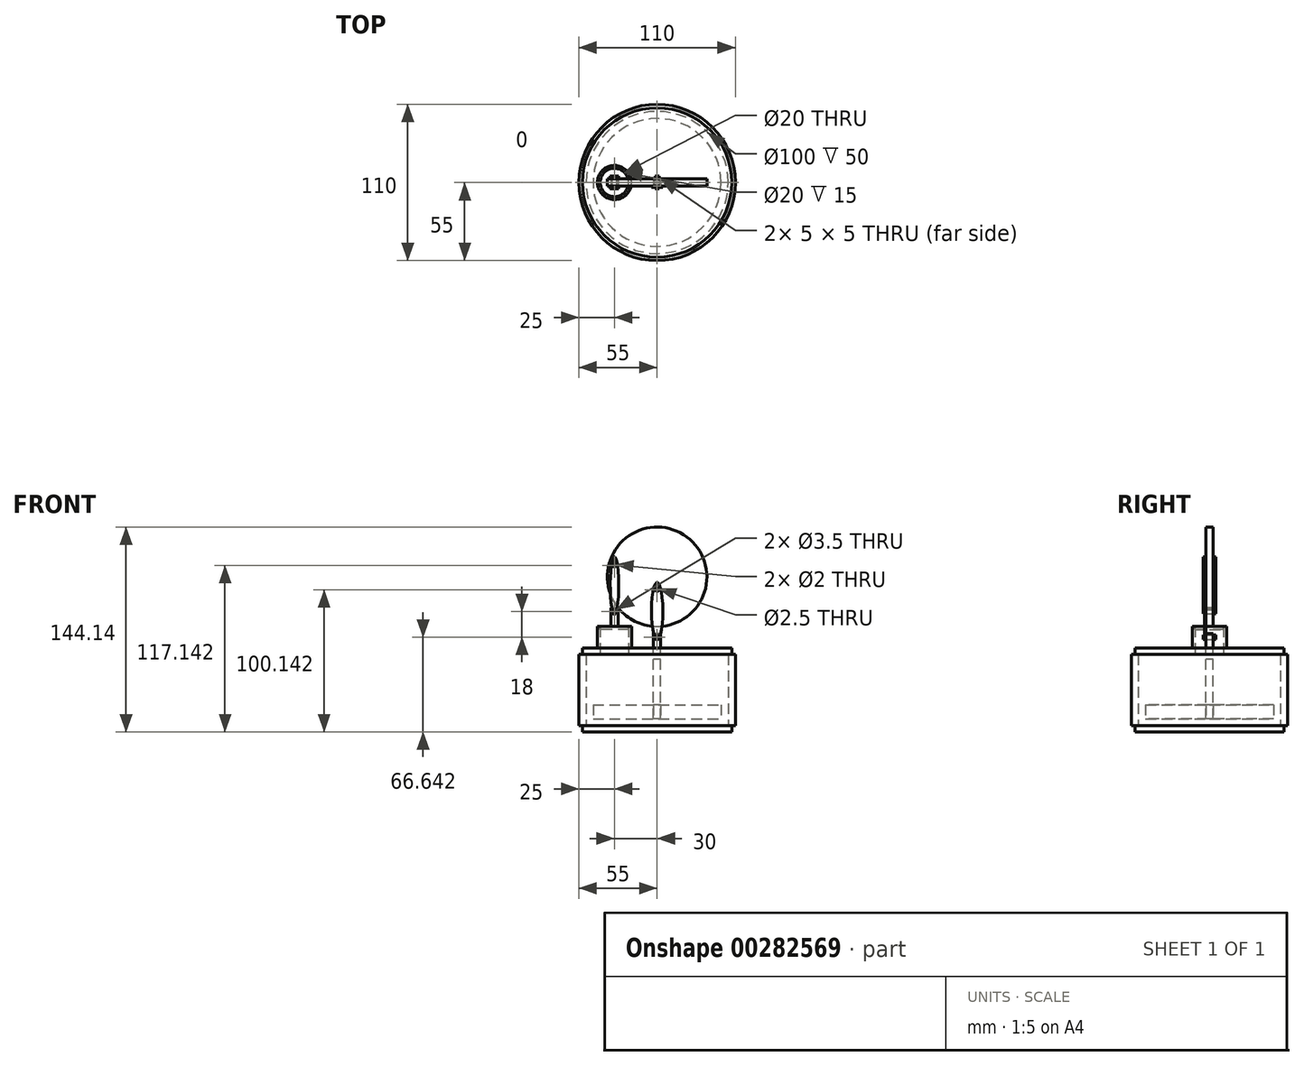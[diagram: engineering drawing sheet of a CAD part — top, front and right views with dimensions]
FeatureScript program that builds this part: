
annotation { "Feature Type Name" : "Feature", "Feature Type Description" : "" }
export const myFeature = defineFeature(function(context is Context, id is Id, definition is map)
    precondition{}
    {
        {
            var Q0;
            Q0=qCreatedBy(makeId("Top.planeOp"),FACE);
            var sketch = newSketch(context, id + "F0", { "sketchPlane" : qUnion([Q0])});
            skCircle(sketch, "E0", {"center": v(0, 0) * mm, "radius": 50 * mm});
            skCircle(sketch, "E1", {"center": v(0, 0) * mm, "radius": 55 * mm});
            skSolve(sketch);
        }
        {
            var Q0;
            Q0=makeQuery(id+"F0.imprint","IMPRINT",FACE,{"disambiguationData":[TD([[makeQuery(id+"F0.imprint","IMPRINT",EDGE,{"derivedFrom":sQuery(id+"F0.wireOp",EDGE,"E0")}),-1.0]])]});
            extrude(context, id + "F1", {"entities" : qUnion([Q0]), "endBound" : BoundingType.SYMMETRIC, "depth" : 50 * mm});
        }
        {
            var Q0;
            Q0=makeQuery(id+"F1.opExtrude","CAP_FACE",FACE,{"disambiguationData":[OSD([sQuery(id+"F0.wireOp",EDGE,"E0"),sQuery(id+"F0.wireOp",EDGE,"E1")])],"isStart":true});
            var sketch = newSketch(context, id + "F2", { "sketchPlane" : qUnion([Q0])});
            skCircle(sketch, "E2", {"center": v(0, 0) * mm, "radius": 52.5 * mm});
            skSolve(sketch);
        }
        {
            var Q0;
            Q0 = qSketchRegion(id + "F2", true);
            extrude(context, id + "F3", {"entities" : qUnion([Q0]), "depth" : 4.57 * mm});
        }
        {
            var Q0;
            Q0=makeQuery(id+"F3.opExtrude","SWEPT_BODY",BODY,{"disambiguationData":[OSD([sQuery(id+"F2.wireOp",EDGE,"E2")])]});
            var Q1;
            Q1=qCreatedBy(makeId("Top.planeOp"),FACE);
            mirror(context, id + "F4", {"entities" : qUnion([Q0]), "mirrorPlane" : qUnion([Q1])});
        }
        {
            var Q0;
            Q0=qCreatedBy(makeId("Front.planeOp"),FACE);
            var sketch = newSketch(context, id + "F5", { "sketchPlane" : qUnion([Q0])});
            skLineSegment(sketch, "E3.bottom", {"start": v(-20, 0) * mm, "end": v(-40, 0) * mm});
            skLineSegment(sketch, "E3.top", {"start": v(-20, 55) * mm, "end": v(-40, 55) * mm});
            skLineSegment(sketch, "E3.left", {"start": v(-20, 0) * mm, "end": v(-20, 55) * mm});
            skLineSegment(sketch, "E3.right", {"start": v(-40, 0) * mm, "end": v(-40, 55) * mm});
            skLineSegment(sketch, "E4", {"start": v(-30, 55) * mm, "end": v(-30, 0) * mm});
            skSolve(sketch);
        }
        {
            var Q0;
            {var subQ0=sQuery(id+"F5.wireOp",EDGE,"E3.right");Q0=makeQuery(id+"F5.imprint","IMPRINT",FACE,{"disambiguationData":[TD([[makeQuery(id+"F5.imprint","IMPRINT",EDGE,{"derivedFrom":subQ0}),-1.0]])]});}
            var Q1;
            Q1=sQuery(id+"F5.wireOp",EDGE,"E4");
            revolve(context, id + "F6", {"operationType" : NewBodyOperationType.REMOVE, "entities" : qUnion([Q0]), "axis" : qUnion([Q1]), "revolveType" : RevolveType.FULL, "oppositeDirection" : true});
        }
        {
            var Q0;
            Q0=makeQuery(id+"F4.opPattern","COPY",FACE,{"derivedFrom":makeQuery(id+"F3.opExtrude","CAP_FACE",FACE,{"disambiguationData":[OSD([sQuery(id+"F2.wireOp",EDGE,"E2")])],"isStart":false}),"instanceName":"1"});
            var sketch = newSketch(context, id + "F7", { "sketchPlane" : qUnion([Q0])});
            skCircle(sketch, "E5", {"center": v(-30, 0) * mm, "radius": 10 * mm});
            skCircle(sketch, "E6", {"center": v(-30, 0) * mm, "radius": 12 * mm});
            skSolve(sketch);
        }
        {
            var Q0;
            Q0=makeQuery(id+"F7.imprint","IMPRINT",FACE,{"disambiguationData":[TD([[makeQuery(id+"F7.imprint","IMPRINT",EDGE,{"derivedFrom":sQuery(id+"F7.wireOp",EDGE,"E5")}),-1.0]])]});
            extrude(context, id + "F8", {"entities" : qUnion([Q0]), "depth" : 15 * mm});
        }
        {
            var Q0;
            Q0=makeQuery(id+"F8.opExtrude","CAP_FACE",FACE,{"disambiguationData":[OSD([sQuery(id+"F7.wireOp",EDGE,"E5"),sQuery(id+"F7.wireOp",EDGE,"E6")])],"isStart":false});
            var sketch = newSketch(context, id + "F9", { "sketchPlane" : qUnion([Q0])});
            skCircle(sketch, "E7", {"center": v(-30, 0) * mm, "radius": 10 * mm});
            skSolve(sketch);
        }
        {
            var Q0;
            Q0 = qSketchRegion(id + "F9", true);
            extrude(context, id + "F10", {"entities" : qUnion([Q0]), "oppositeDirection" : true, "depth" : 2 * mm});
        }
        {
            var Q0;
            Q0=makeQuery(id+"F4.opPattern","COPY",FACE,{"derivedFrom":makeQuery(id+"F3.opExtrude","CAP_FACE",FACE,{"disambiguationData":[OSD([sQuery(id+"F2.wireOp",EDGE,"E2")])],"isStart":false}),"instanceName":"1"});
            var sketch = newSketch(context, id + "F11", { "sketchPlane" : qUnion([Q0])});
            skLineSegment(sketch, "E8.bottom", {"start": v(2.5, 2.5) * mm, "end": v(-2.5, 2.5) * mm});
            skLineSegment(sketch, "E8.top", {"start": v(2.5, -2.5) * mm, "end": v(-2.5, -2.5) * mm});
            skLineSegment(sketch, "E8.left", {"start": v(2.5, 2.5) * mm, "end": v(2.5, -2.5) * mm});
            skLineSegment(sketch, "E8.right", {"start": v(-2.5, 2.5) * mm, "end": v(-2.5, -2.5) * mm});
            skPoint(sketch, "E8.middle", {"position": v(0, 0) * mm});
            skSolve(sketch);
        }
        {
            var Q0;
            Q0=makeQuery(id+"F11.imprint","IMPRINT",FACE,{"disambiguationData":[TD([[makeQuery(id+"F11.imprint","IMPRINT",EDGE,{"derivedFrom":sQuery(id+"F11.wireOp",EDGE,"E8.bottom")}),1.0]])]});
            extrude(context, id + "F12", {"entities" : qUnion([Q0]), "operationType" : NewBodyOperationType.REMOVE, "oppositeDirection" : true, "depth" : 25 * mm});
        }
        {
            var Q0;
            Q0 = qSketchRegion(id + "F11", true);
            extrude(context, id + "F13", {"entities" : qUnion([Q0]), "oppositeDirection" : true, "depth" : 50 * mm, "hasSecondDirection" : true, "secondDirectionOppositeDirection" : false, "secondDirectionDepth" : 10 * mm});
        }
        {
            var Q0;
            Q0=makeQuery(id+"F13.opExtrude","CAP_FACE",FACE,{"disambiguationData":[OSD([sQuery(id+"F11.wireOp",EDGE,"E8.bottom"),sQuery(id+"F11.wireOp",EDGE,"E8.top"),sQuery(id+"F11.wireOp",EDGE,"E8.left"),sQuery(id+"F11.wireOp",EDGE,"E8.right")])],"isStart":false});
            var sketch = newSketch(context, id + "F14", { "sketchPlane" : qUnion([Q0])});
            skCircle(sketch, "E9", {"center": v(0, 0) * mm, "radius": 45 * mm});
            skSolve(sketch);
        }
        {
            var Q0;
            Q0=makeQuery(id+"F14.imprint","IMPRINT",FACE,{"disambiguationData":[TD([[makeQuery(id+"F14.imprint","IMPRINT",EDGE,{"derivedFrom":sQuery(id+"F14.wireOp",EDGE,"E9")}),1.0]])]});
            extrude(context, id + "F15", {"entities" : qUnion([Q0]), "oppositeDirection" : true, "depth" : 10 * mm});
        }
        {
            var Q0;
            Q0=makeQuery(id+"F13.opExtrude","SWEPT_FACE",FACE,{"disambiguationData":[OSD([sQuery(id+"F11.wireOp",EDGE,"E8.top")])]});
            var sketch = newSketch(context, id + "F16", { "sketchPlane" : qUnion([Q0])});
            skLineSegment(sketch, "E10.bottom", {"start": v(-2.5, 39.57) * mm, "end": v(2.5, 39.57) * mm});
            skLineSegment(sketch, "E10.top", {"start": v(-2.5, 34.57) * mm, "end": v(2.5, 34.57) * mm});
            skLineSegment(sketch, "E10.left", {"start": v(-2.5, 39.57) * mm, "end": v(-2.5, 34.57) * mm});
            skLineSegment(sketch, "E10.right", {"start": v(2.5, 39.57) * mm, "end": v(2.5, 34.57) * mm});
            skCircle(sketch, "E11", {"center": v(0, 37.07) * mm, "radius": 1.75 * mm});
            skCircle(sketch, "E12", {"center": v(0, 37.07) * mm, "radius": 1.5 * mm});
            skSolve(sketch);
        }
        {
            var Q0;
            Q0=makeQuery(id+"F16.imprint","IMPRINT",FACE,{"disambiguationData":[TD([[makeQuery(id+"F16.imprint","IMPRINT",EDGE,{"derivedFrom":sQuery(id+"F16.wireOp",EDGE,"E11")}),1.0]])]});
            var Q1;
            Q1=makeQuery(id+"F16.imprint","IMPRINT",FACE,{"disambiguationData":[TD([[makeQuery(id+"F16.imprint","IMPRINT",EDGE,{"derivedFrom":sQuery(id+"F16.wireOp",EDGE,"E12")}),1.0]])]});
            extrude(context, id + "F17", {"entities" : qUnion([Q0, Q1]), "operationType" : NewBodyOperationType.REMOVE, "oppositeDirection" : true, "depth" : 25 * mm});
        }
        {
            var Q0;
            Q0=makeQuery(id+"F16.imprint","IMPRINT",FACE,{"disambiguationData":[TD([[makeQuery(id+"F16.imprint","IMPRINT",EDGE,{"derivedFrom":sQuery(id+"F16.wireOp",EDGE,"E12")}),1.0]])]});
            extrude(context, id + "F18", {"entities" : qUnion([Q0]), "depth" : 2 * mm, "hasSecondDirection" : true, "secondDirectionOppositeDirection" : true, "secondDirectionDepth" : 7 * mm});
        }
        {
            var Q0;
            Q0=makeQuery(id+"F10.opExtrude","CAP_FACE",FACE,{"disambiguationData":[OSD([sQuery(id+"F9.wireOp",EDGE,"E7")])],"isStart":true});
            var sketch = newSketch(context, id + "F19", { "sketchPlane" : qUnion([Q0])});
            skLineSegment(sketch, "E13.bottom", {"start": v(-32.5, 2.5) * mm, "end": v(-27.5, 2.5) * mm});
            skLineSegment(sketch, "E13.top", {"start": v(-32.5, -2.5) * mm, "end": v(-27.5, -2.5) * mm});
            skLineSegment(sketch, "E13.left", {"start": v(-32.5, 2.5) * mm, "end": v(-32.5, -2.5) * mm});
            skLineSegment(sketch, "E13.right", {"start": v(-27.5, 2.5) * mm, "end": v(-27.5, -2.5) * mm});
            skPoint(sketch, "E13.middle", {"position": v(-30, 0) * mm});
            skSolve(sketch);
        }
        {
            var Q0;
            Q0 = qSketchRegion(id + "F19", true);
            extrude(context, id + "F20", {"entities" : qUnion([Q0]), "operationType" : NewBodyOperationType.ADD, "depth" : 13 * mm});
        }
        {
            var Q0;
            Q0=makeQuery(id+"F20.opExtrude","SWEPT_FACE",FACE,{"disambiguationData":[OSD([sQuery(id+"F19.wireOp",EDGE,"E13.top")])]});
            var sketch = newSketch(context, id + "F21", { "sketchPlane" : qUnion([Q0])});
            skLineSegment(sketch, "E14.bottom", {"start": v(-32.5, 57.57) * mm, "end": v(-27.5, 57.57) * mm});
            skLineSegment(sketch, "E14.top", {"start": v(-32.5, 52.57) * mm, "end": v(-27.5, 52.57) * mm});
            skLineSegment(sketch, "E14.left", {"start": v(-32.5, 57.57) * mm, "end": v(-32.5, 52.57) * mm});
            skLineSegment(sketch, "E14.right", {"start": v(-27.5, 57.57) * mm, "end": v(-27.5, 52.57) * mm});
            skCircle(sketch, "E15", {"center": v(-30, 55.07) * mm, "radius": 1.75 * mm});
            skPoint(sketch, "E15.centerSnap0", {"position": v(-30, 52.57) * mm});
            skCircle(sketch, "E16", {"center": v(-30, 55.07) * mm, "radius": 1.5 * mm});
            skSolve(sketch);
        }
        {
            var Q0;
            Q0=makeQuery(id+"F21.imprint","IMPRINT",FACE,{"disambiguationData":[TD([[makeQuery(id+"F21.imprint","IMPRINT",EDGE,{"derivedFrom":sQuery(id+"F21.wireOp",EDGE,"E15")}),1.0]])]});
            var Q1;
            Q1=makeQuery(id+"F21.imprint","IMPRINT",FACE,{"disambiguationData":[TD([[makeQuery(id+"F21.imprint","IMPRINT",EDGE,{"derivedFrom":sQuery(id+"F21.wireOp",EDGE,"E16")}),1.0]])]});
            extrude(context, id + "F22", {"entities" : qUnion([Q0, Q1]), "operationType" : NewBodyOperationType.REMOVE, "oppositeDirection" : true, "depth" : 25 * mm});
        }
        {
            var Q0;
            Q0=makeQuery(id+"F21.imprint","IMPRINT",FACE,{"disambiguationData":[TD([[makeQuery(id+"F21.imprint","IMPRINT",EDGE,{"derivedFrom":sQuery(id+"F21.wireOp",EDGE,"E16")}),1.0]])]});
            extrude(context, id + "F23", {"entities" : qUnion([Q0]), "depth" : 2 * mm, "hasSecondDirection" : true, "secondDirectionOppositeDirection" : true, "secondDirectionDepth" : 7 * mm});
        }
        {
            var Q0;
            Q0=makeQuery(id+"F23.opExtrude","CAP_FACE",FACE,{"disambiguationData":[OSD([sQuery(id+"F21.wireOp",EDGE,"E16")])],"isStart":false});
            var sketch = newSketch(context, id + "F24", { "sketchPlane" : qUnion([Q0])});
            skEllipse(sketch, "E17", {"center": v(-30, 73.57) * mm, "majorRadius": 20 * mm, "minorRadius": 3 * mm, "majorAxis": v(0, -1)});
            skCircle(sketch, "E18", {"center": v(-30, 87.57) * mm, "radius": 1 * mm});
            skPoint(sketch, "E19", {"position": v(-30, 93.57) * mm});
            skPoint(sketch, "E20", {"position": v(-30, 53.57) * mm});
            skSolve(sketch);
        }
        {
            var Q0;
            Q0=makeQuery(id+"F24.imprint","IMPRINT",FACE,{"disambiguationData":[TD([[makeQuery(id+"F24.imprint","IMPRINT",EDGE,{"derivedFrom":sQuery(id+"F24.wireOp",EDGE,"E18")}),-1.0]])]});
            extrude(context, id + "F25", {"entities" : qUnion([Q0]), "oppositeDirection" : true, "depth" : 1 * mm});
        }
        {
            var Q0;
            Q0=makeQuery(id+"F25.opExtrude","SWEPT_BODY",BODY,{"disambiguationData":[OSD([sQuery(id+"F21.wireOp",EDGE,"E16"),sQuery(id+"F24.wireOp",EDGE,"E17")])]});
            var Q1;
            Q1=qCreatedBy(makeId("Front.planeOp"),FACE);
            mirror(context, id + "F26", {"operationType" : NewBodyOperationType.ADD, "entities" : qUnion([Q0]), "mirrorPlane" : qUnion([Q1])});
        }
        {
            var Q0;
            Q0=makeQuery(id+"F4.opPattern","COPY",FACE,{"derivedFrom":makeQuery(id+"F3.opExtrude","CAP_FACE",FACE,{"disambiguationData":[OSD([sQuery(id+"F2.wireOp",EDGE,"E2")])],"isStart":false}),"instanceName":"1"});
            var sketch = newSketch(context, id + "F27", { "sketchPlane" : qUnion([Q0])});
            skLineSegment(sketch, "E21.bottom", {"start": v(-2.5, 2.5) * mm, "end": v(2.5, 2.5) * mm});
            skLineSegment(sketch, "E21.top", {"start": v(-2.5, -2.5) * mm, "end": v(2.5, -2.5) * mm});
            skLineSegment(sketch, "E21.left", {"start": v(-2.5, 2.5) * mm, "end": v(-2.5, -2.5) * mm});
            skLineSegment(sketch, "E21.right", {"start": v(2.5, 2.5) * mm, "end": v(2.5, -2.5) * mm});
            skPoint(sketch, "E21.middle", {"position": v(0, 0) * mm});
            skSolve(sketch);
        }
        {
            var Q0;
            Q0 = qSketchRegion(id + "F27", true);
            extrude(context, id + "F28", {"entities" : qUnion([Q0]), "operationType" : NewBodyOperationType.REMOVE, "oppositeDirection" : true, "depth" : 8 * mm});
        }
        {
            var Q0;
            Q0=makeQuery(id+"F18.opExtrude","CAP_FACE",FACE,{"disambiguationData":[OSD([sQuery(id+"F16.wireOp",EDGE,"E12")])],"isStart":false});
            var sketch = newSketch(context, id + "F29", { "sketchPlane" : qUnion([Q0])});
            skEllipse(sketch, "E22", {"center": v(0, 55.57) * mm, "majorRadius": 20 * mm, "minorRadius": 4 * mm, "majorAxis": v(0, -1)});
            skPoint(sketch, "E23", {"position": v(0, 35.57) * mm});
            skCircle(sketch, "E24", {"center": v(0, 70.57) * mm, "radius": 1.25 * mm});
            skPoint(sketch, "E25", {"position": v(0, 75.57) * mm});
            skSolve(sketch);
        }
        {
            var Q0;
            Q0=makeQuery(id+"F29.imprint","IMPRINT",FACE,{"disambiguationData":[TD([[makeQuery(id+"F29.imprint","IMPRINT",EDGE,{"derivedFrom":sQuery(id+"F29.wireOp",EDGE,"E24")}),-1.0]])]});
            extrude(context, id + "F30", {"entities" : qUnion([Q0]), "operationType" : NewBodyOperationType.ADD, "oppositeDirection" : true, "depth" : 1.9 * mm, "hasSecondDirection" : true, "secondDirectionOppositeDirection" : true, "secondDirectionDepth" : 1.1 * mm});
        }
        {
            var Q0;
            Q0=qCreatedBy(makeId("Front.planeOp"),FACE);
            var sketch = newSketch(context, id + "F31", { "sketchPlane" : qUnion([Q0])});
            skCircle(sketch, "E26", {"center": v(0, 79.57) * mm, "radius": 35 * mm});
            skSolve(sketch);
        }
        {
            var Q0;
            Q0 = qSketchRegion(id + "F31", true);
            extrude(context, id + "F32", {"entities" : qUnion([Q0]), "endBound" : BoundingType.SYMMETRIC, "depth" : 5 * mm});
        }
    });
